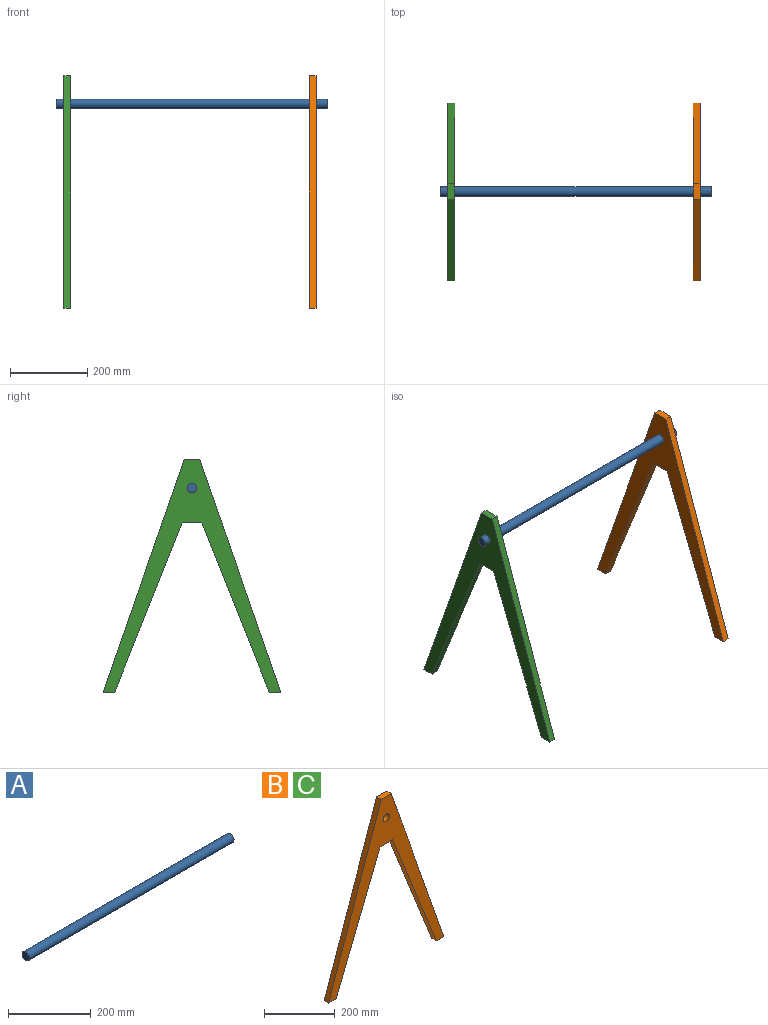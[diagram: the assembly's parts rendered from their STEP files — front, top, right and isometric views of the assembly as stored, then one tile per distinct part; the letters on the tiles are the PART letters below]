
ASSEMBLY  parts=3 mates=2
PART A: 3 faces, bbox 700x25x25 mm
  f0: cylinder r=12.5mm len=700mm, axis (-1,0,0), area 54977.9mm2, adj f1,f2
  f1: plane 25x25mm, normal (1,0,0), area 490.9mm2, adj f0
  f2: plane 25x25mm, normal (-1,0,0), area 490.9mm2, adj f0
PART B: 11 faces, bbox 460x18x600 mm
  f0: plane 600x210mm, normal (-0.94,0,0.33), area 11442.4mm2, adj f1,f8,f9,f10
  f1: plane 30x18mm, normal (0,0,-1), area 540mm2, adj f0,f2,f9,f10
  f2: plane 437.63x175mm, normal (0.93,0,-0.37), area 8483.8mm2, adj f1,f3,f9,f10
  f3: plane 50x18mm, normal (0,0,-1), area 900mm2, adj f2,f4,f9,f10
  f4: plane 437.63x175mm, normal (-0.93,0,-0.37), area 8483.8mm2, adj f3,f5,f9,f10
  f5: plane 30x18mm, normal (0,0,-1), area 540mm2, adj f4,f6,f9,f10
  f6: plane 600x210mm, normal (0.94,0,0.33), area 11442.4mm2, adj f5,f8,f9,f10
  f7: cylinder r=12.5mm len=25mm, axis (0,1,0), area 1413.7mm2, adj f9,f10
  f8: plane 40x18mm, normal (0,0,1), area 720mm2, adj f0,f6,f9,f10
  f9: plane 600x460mm, normal (0,-1,0), area 51042.2mm2, adj f0,f1,f2,f3,f4,f5,f6,f7
  f10: plane 600x460mm, normal (0,1,0), area 51042.2mm2, adj f0,f1,f2,f3,f4,f5,f6,f7
PART C: same geometry as B
PLACE A t=(210.23,447.44,74.44)mm
PLACE B rot(axis=(0,0,-1),90deg) t=(881.21,544.03,75.45)mm
PLACE C rot(axis=(0,0,-1),90deg) t=(246.66,544.03,75.45)mm
MATE slider A.f0 <-> B.f7  axis (1,0,0) through (910.23,447.44,90.98)mm
MATE slider C.f7 <-> A.f0  axis (1,0,0) through (246.66,447.44,90.98)mm
